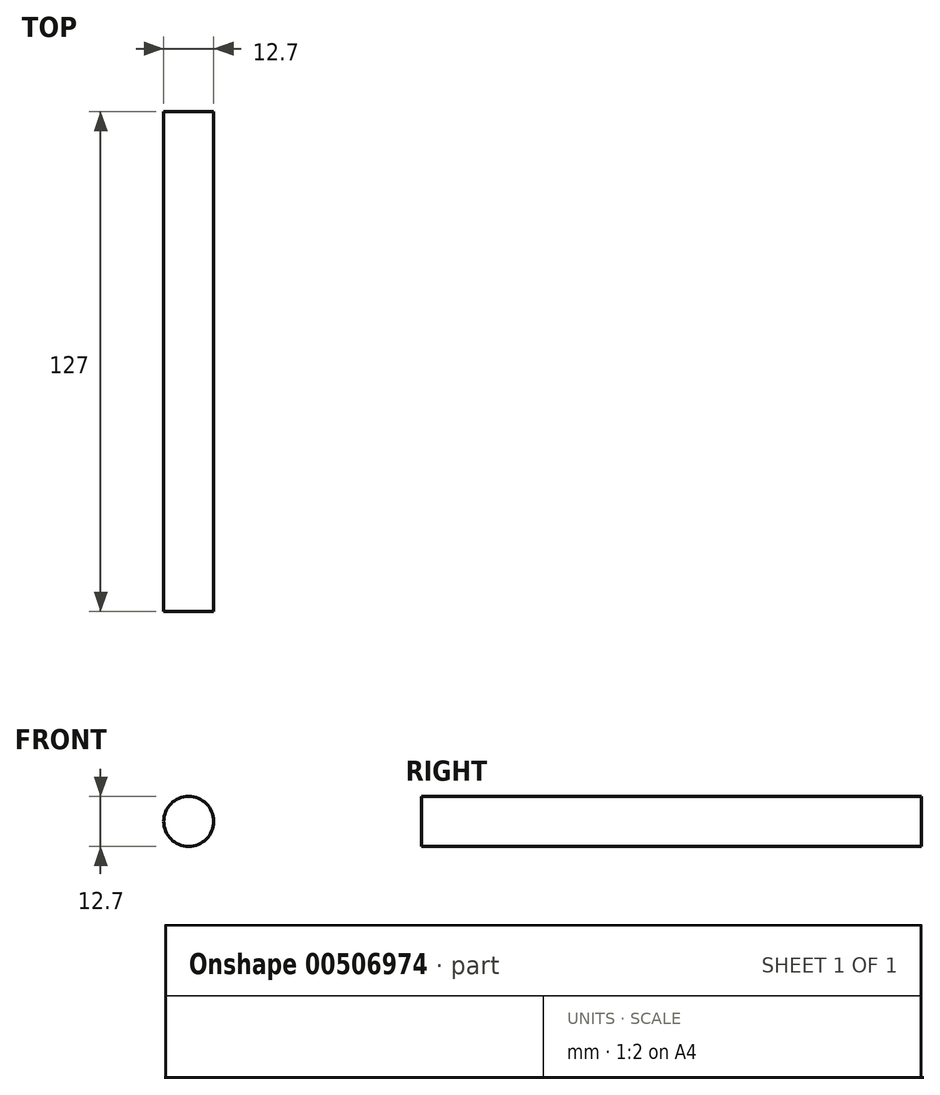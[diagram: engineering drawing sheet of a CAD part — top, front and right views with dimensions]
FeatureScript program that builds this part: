
annotation { "Feature Type Name" : "Feature", "Feature Type Description" : "" }
export const myFeature = defineFeature(function(context is Context, id is Id, definition is map)
    precondition{}
    {
        {
            var Q0;
            Q0=qCreatedBy(makeId("Front.planeOp"),FACE);
            var sketch = newSketch(context, id + "F0", { "sketchPlane" : qUnion([Q0])});
            skCircle(sketch, "E0", {"center": v(0, 0) * mm, "radius": 6.35 * mm});
            skSolve(sketch);
        }
        {
            var Q0;
            Q0=makeQuery(id+"F0.imprint","IMPRINT",FACE,{"disambiguationData":[TD([[makeQuery(id+"F0.imprint","IMPRINT",EDGE,{"derivedFrom":sQuery(id+"F0.wireOp",EDGE,"E0")}),1.0]])]});
            var Q1;
            Q1=sQuery(id+"F0.wireOp",EDGE,"E0");
            extrude(context, id + "F1", {"entities" : qUnion([Q0]), "surfaceEntities" : qUnion([Q1]), "depth" : 127 * mm, "offsetDistance" : 25.4 * mm});
        }
    });
